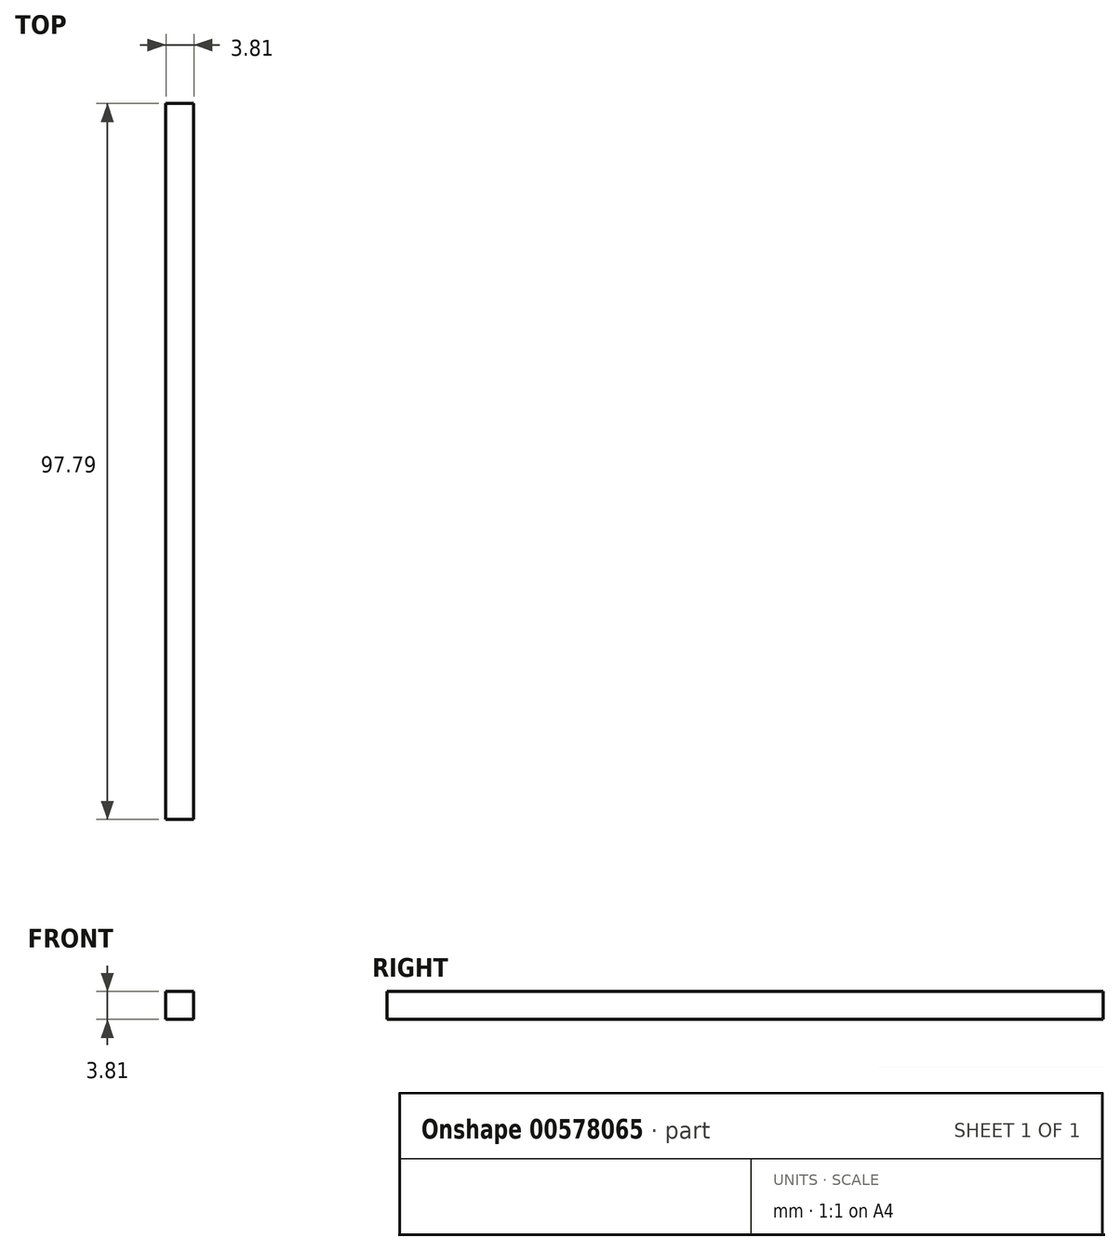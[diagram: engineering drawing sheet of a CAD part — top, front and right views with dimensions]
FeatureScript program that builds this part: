
annotation { "Feature Type Name" : "Feature", "Feature Type Description" : "" }
export const myFeature = defineFeature(function(context is Context, id is Id, definition is map)
    precondition{}
    {
        {
            var Q0;
            Q0=qCreatedBy(makeId("Top.planeOp"),FACE);
            var sketch = newSketch(context, id + "F0", { "sketchPlane" : qUnion([Q0])});
            skLineSegment(sketch, "E0.bottom", {"start": v(30.48, 129.14) * mm, "end": v(34.29, 129.14) * mm});
            skLineSegment(sketch, "E0.top", {"start": v(30.48, 31.35) * mm, "end": v(34.29, 31.35) * mm});
            skLineSegment(sketch, "E0.left", {"start": v(30.48, 129.14) * mm, "end": v(30.48, 31.35) * mm});
            skLineSegment(sketch, "E0.right", {"start": v(34.29, 129.14) * mm, "end": v(34.29, 31.35) * mm});
            skSolve(sketch);
        }
        {
            var Q0;
            Q0 = qSketchRegion(id + "F0", true);
            extrude(context, id + "F1", {"entities" : qUnion([Q0]), "depth" : 3.8 * mm, "offsetDistance" : 25.4 * mm});
        }
    });
